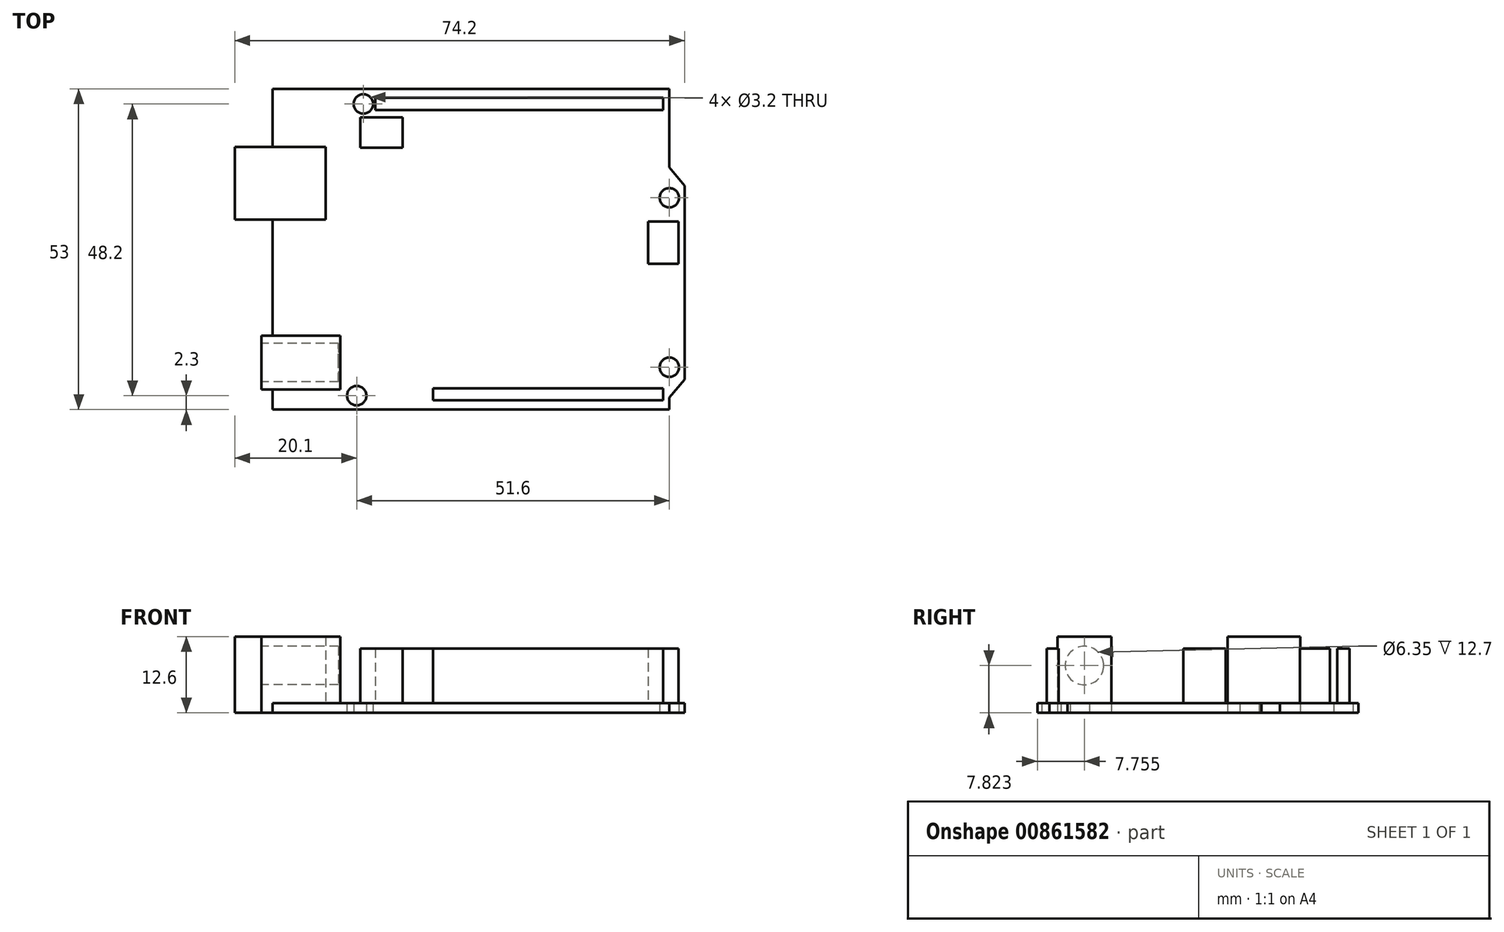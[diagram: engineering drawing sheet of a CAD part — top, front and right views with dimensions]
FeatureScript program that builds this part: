
annotation { "Feature Type Name" : "Feature", "Feature Type Description" : "" }
export const myFeature = defineFeature(function(context is Context, id is Id, definition is map)
    precondition{}
    {
        {
            var Q0;
            Q0=qCreatedBy(makeId("Top.planeOp"),FACE);
            var sketch = newSketch(context, id + "F0", { "sketchPlane" : qUnion([Q0])});
            skLineSegment(sketch, "E0.bottom", {"start": v(31.5, 26.5) * mm, "end": v(-34, 26.5) * mm});
            skLineSegment(sketch, "E0.top", {"start": v(31.5, -26.5) * mm, "end": v(-34, -26.5) * mm});
            skLineSegment(sketch, "E0.left", {"start": v(34, 10.5) * mm, "end": v(34, -21.5) * mm});
            skLineSegment(sketch, "E0.right", {"start": v(-34, 26.5) * mm, "end": v(-34, -26.5) * mm});
            skPoint(sketch, "E0.middle", {"position": v(0, 0) * mm});
            skLineSegment(sketch, "E1.bottom", {"start": v(-34, 26.5) * mm, "end": v(31.5, 26.5) * mm});
            skLineSegment(sketch, "E1.top", {"start": v(-34, -26.5) * mm, "end": v(31.5, -26.5) * mm});
            skLineSegment(sketch, "E1.right", {"start": v(31.5, 26.5) * mm, "end": v(31.5, 13.5) * mm});
            skPoint(sketch, "E2", {"position": v(31.5, -24.5) * mm});
            skPoint(sketch, "E3", {"position": v(34, -21.5) * mm});
            skPoint(sketch, "E4", {"position": v(34, 10.5) * mm});
            skPoint(sketch, "E5", {"position": v(31.5, 13.5) * mm});
            skPoint(sketch, "E6.orphan", {"position": v(34, 26.5) * mm});
            skPoint(sketch, "E7.orphan", {"position": v(34, -26.5) * mm});
            skLineSegment(sketch, "E8", {"start": v(31.5, -24.5) * mm, "end": v(34, -21.5) * mm});
            skLineSegment(sketch, "E9", {"start": v(34, 10.5) * mm, "end": v(31.5, 13.5) * mm});
            skLineSegment(sketch, "E10.trimOffspring", {"start": v(31.5, -24.5) * mm, "end": v(31.5, -26.5) * mm});
            skCircle(sketch, "E11", {"center": v(-19, 24) * mm, "radius": 1.6 * mm});
            skCircle(sketch, "E12", {"center": v(31.5, 8.5) * mm, "radius": 1.6 * mm});
            skCircle(sketch, "E13", {"center": v(31.5, -19.5) * mm, "radius": 1.6 * mm});
            skCircle(sketch, "E14", {"center": v(-20.1, -24.2) * mm, "radius": 1.6 * mm});
            skLineSegment(sketch, "E15.bottom", {"start": v(30.5, 23) * mm, "end": v(-17, 23) * mm});
            skLineSegment(sketch, "E15.top", {"start": v(30.5, 25) * mm, "end": v(-17, 25) * mm});
            skLineSegment(sketch, "E15.left", {"start": v(30.5, 23) * mm, "end": v(30.5, 25) * mm});
            skLineSegment(sketch, "E15.right", {"start": v(-17, 23) * mm, "end": v(-17, 25) * mm});
            skPoint(sketch, "E15.middle", {"position": v(6.75, 24) * mm});
            skLineSegment(sketch, "E16.bottom", {"start": v(30.5, -24.96) * mm, "end": v(-7.5, -24.96) * mm});
            skLineSegment(sketch, "E16.top", {"start": v(30.5, -22.96) * mm, "end": v(-7.5, -22.96) * mm});
            skLineSegment(sketch, "E16.left", {"start": v(30.5, -24.96) * mm, "end": v(30.5, -22.96) * mm});
            skLineSegment(sketch, "E16.right", {"start": v(-7.5, -24.96) * mm, "end": v(-7.5, -22.96) * mm});
            skPoint(sketch, "E16.middle", {"position": v(11.5, -23.96) * mm});
            skLineSegment(sketch, "E17.bottom", {"start": v(-40.2, 16.9) * mm, "end": v(-25.2, 16.9) * mm});
            skLineSegment(sketch, "E17.top", {"start": v(-40.2, 4.9) * mm, "end": v(-25.2, 4.9) * mm});
            skLineSegment(sketch, "E17.left", {"start": v(-40.2, 16.9) * mm, "end": v(-40.2, 4.9) * mm});
            skLineSegment(sketch, "E17.right", {"start": v(-25.2, 16.9) * mm, "end": v(-25.2, 4.9) * mm});
            skLineSegment(sketch, "E18.bottom", {"start": v(-35.8, -14.3) * mm, "end": v(-22.8, -14.3) * mm});
            skLineSegment(sketch, "E18.top", {"start": v(-35.8, -23.2) * mm, "end": v(-22.8, -23.2) * mm});
            skLineSegment(sketch, "E18.left", {"start": v(-35.8, -14.3) * mm, "end": v(-35.8, -23.2) * mm});
            skLineSegment(sketch, "E18.right", {"start": v(-22.8, -14.3) * mm, "end": v(-22.8, -23.2) * mm});
            skLineSegment(sketch, "E19.bottom", {"start": v(33, -2.4) * mm, "end": v(28, -2.4) * mm});
            skLineSegment(sketch, "E19.top", {"start": v(33, 4.6) * mm, "end": v(28, 4.6) * mm});
            skLineSegment(sketch, "E19.left", {"start": v(33, -2.4) * mm, "end": v(33, 4.6) * mm});
            skLineSegment(sketch, "E19.right", {"start": v(28, -2.4) * mm, "end": v(28, 4.6) * mm});
            skLineSegment(sketch, "E20.bottom", {"start": v(-19.5, 16.8) * mm, "end": v(-12.5, 16.8) * mm});
            skLineSegment(sketch, "E20.top", {"start": v(-19.5, 21.8) * mm, "end": v(-12.5, 21.8) * mm});
            skLineSegment(sketch, "E20.left", {"start": v(-19.5, 16.8) * mm, "end": v(-19.5, 21.8) * mm});
            skLineSegment(sketch, "E20.right", {"start": v(-12.5, 16.8) * mm, "end": v(-12.5, 21.8) * mm});
            skSolve(sketch);
        }
        {
            var Q0;
            Q0=makeQuery(id+"F0.imprint","IMPRINT",FACE,{"disambiguationData":[TD([[makeQuery(id+"F0.imprint","IMPRINT",EDGE,{"derivedFrom":sQuery(id+"F0.wireOp",EDGE,"E0.bottom")}),1.0]])]});
            var Q1;
            Q1=makeQuery(id+"F0.imprint","IMPRINT",FACE,{"disambiguationData":[TD([[makeQuery(id+"F0.imprint","IMPRINT",EDGE,{"derivedFrom":sQuery(id+"F0.wireOp",EDGE,"E0.left")}),-1.0]])]});
            extrude(context, id + "F1", {"entities" : qUnion([Q0, Q1]), "depth" : 1.6 * mm, "offsetDistance" : 25 * mm});
        }
        {
            var Q0;
            {var subQ5=sQuery(id+"F0.wireOp",EDGE,"E17.left");Q0=makeQuery(id+"F0.imprint","IMPRINT",FACE,{"disambiguationData":[TD([[makeQuery(id+"F0.imprint","IMPRINT",EDGE,{"derivedFrom":subQ5}),1.0]])]});}
            var Q1;
            {var subQ5=sQuery(id+"F0.wireOp",EDGE,"E17.right");Q1=makeQuery(id+"F0.imprint","IMPRINT",FACE,{"disambiguationData":[TD([[makeQuery(id+"F0.imprint","IMPRINT",EDGE,{"derivedFrom":subQ5}),-1.0]])]});}
            var Q2;
            {var subQ5=sQuery(id+"F0.wireOp",EDGE,"E18.left");Q2=makeQuery(id+"F0.imprint","IMPRINT",FACE,{"disambiguationData":[TD([[makeQuery(id+"F0.imprint","IMPRINT",EDGE,{"derivedFrom":subQ5}),1.0]])]});}
            var Q3;
            {var subQ5=sQuery(id+"F0.wireOp",EDGE,"E18.right");Q3=makeQuery(id+"F0.imprint","IMPRINT",FACE,{"disambiguationData":[TD([[makeQuery(id+"F0.imprint","IMPRINT",EDGE,{"derivedFrom":subQ5}),-1.0]])]});}
            extrude(context, id + "F2", {"entities" : qUnion([Q0, Q1, Q2, Q3]), "operationType" : NewBodyOperationType.ADD, "depth" : (1.6 + 11) * mm, "offsetDistance" : 25 * mm});
        }
        {
            var Q0;
            Q0=makeQuery(id+"F0.imprint","IMPRINT",FACE,{"disambiguationData":[TD([[makeQuery(id+"F0.imprint","IMPRINT",EDGE,{"derivedFrom":sQuery(id+"F0.wireOp",EDGE,"E15.bottom")}),-1.0]])]});
            var Q1;
            Q1=makeQuery(id+"F0.imprint","IMPRINT",FACE,{"disambiguationData":[TD([[makeQuery(id+"F0.imprint","IMPRINT",EDGE,{"derivedFrom":sQuery(id+"F0.wireOp",EDGE,"E16.bottom")}),-1.0]])]});
            var Q2;
            Q2=makeQuery(id+"F0.imprint","IMPRINT",FACE,{"disambiguationData":[TD([[makeQuery(id+"F0.imprint","IMPRINT",EDGE,{"derivedFrom":sQuery(id+"F0.wireOp",EDGE,"E20.bottom")}),1.0]])]});
            var Q3;
            Q3=makeQuery(id+"F0.imprint","IMPRINT",FACE,{"disambiguationData":[TD([[makeQuery(id+"F0.imprint","IMPRINT",EDGE,{"derivedFrom":sQuery(id+"F0.wireOp",EDGE,"E19.bottom")}),-1.0]])]});
            extrude(context, id + "F3", {"entities" : qUnion([Q0, Q1, Q2, Q3]), "operationType" : NewBodyOperationType.ADD, "depth" : 10.6 * mm, "offsetDistance" : 25 * mm});
        }
        {
            var Q0;
            Q0=makeQuery(id+"F2.opExtrude","SWEPT_FACE",FACE,{"disambiguationData":[OSD([sQuery(id+"F0.wireOp",EDGE,"E18.left")])]});
            var sketch = newSketch(context, id + "F4", { "sketchPlane" : qUnion([Q0])});
            skCircle(sketch, "E21", {"center": v(18.74, 7.82) * mm, "radius": 3.18 * mm});
            skSolve(sketch);
        }
        {
            var Q0;
            Q0=makeQuery(id+"F4.imprint","IMPRINT",FACE,{"disambiguationData":[TD([[makeQuery(id+"F4.imprint","IMPRINT",EDGE,{"derivedFrom":sQuery(id+"F4.wireOp",EDGE,"E21")}),1.0]])]});
            extrude(context, id + "F5", {"entities" : qUnion([Q0]), "operationType" : NewBodyOperationType.REMOVE, "oppositeDirection" : true, "depth" : 12.7 * mm, "offsetDistance" : 25 * mm});
        }
    });
